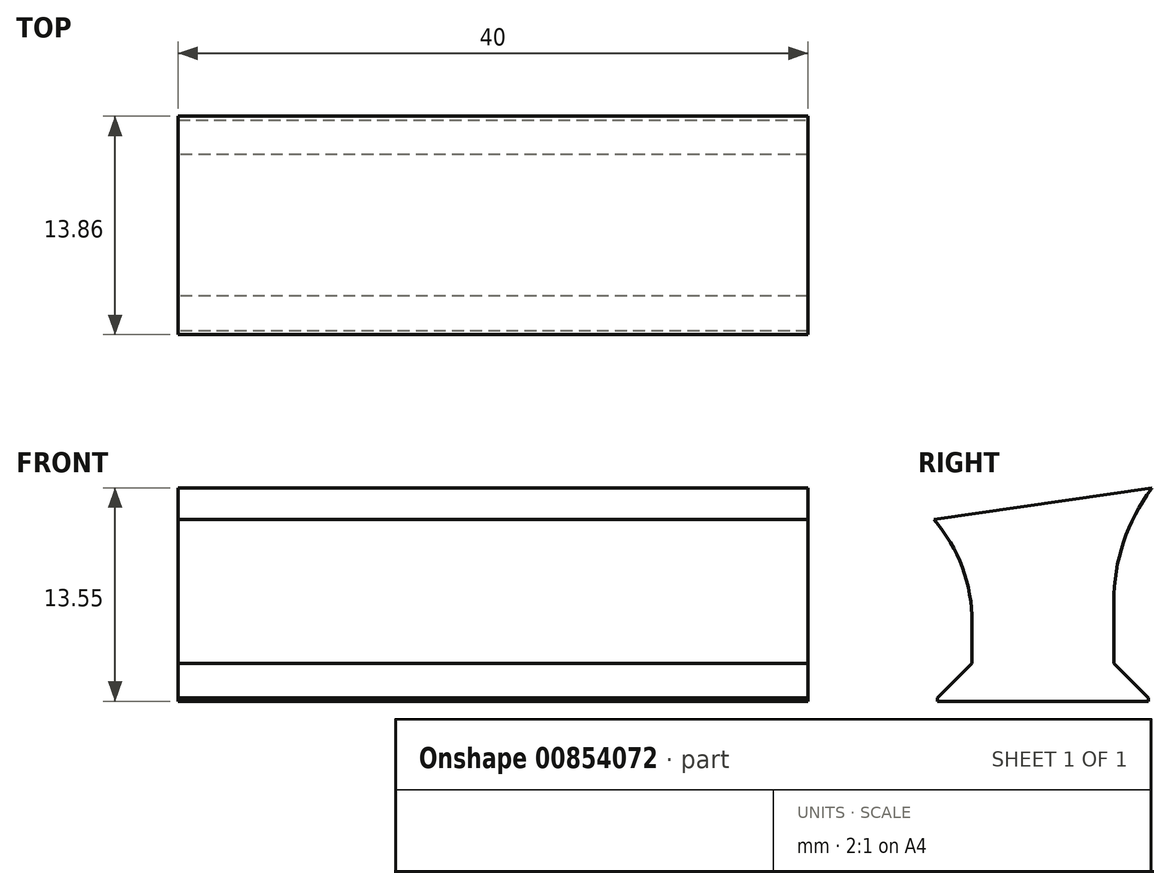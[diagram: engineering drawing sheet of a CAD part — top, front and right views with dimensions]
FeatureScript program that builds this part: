
annotation { "Feature Type Name" : "Feature", "Feature Type Description" : "" }
export const myFeature = defineFeature(function(context is Context, id is Id, definition is map)
    precondition{}
    {
        {
            var Q0;
            Q0=qCreatedBy(makeId("Top.planeOp"),FACE);
            var sketch = newSketch(context, id + "F0", { "sketchPlane" : qUnion([Q0])});
            skLineSegment(sketch, "E0.bottom", {"start": v(0, 0) * mm, "end": v(40, 0) * mm});
            skLineSegment(sketch, "E0.top", {"start": v(0, 13.4) * mm, "end": v(40, 13.4) * mm});
            skLineSegment(sketch, "E0.left", {"start": v(0, 0) * mm, "end": v(0, 13.4) * mm});
            skLineSegment(sketch, "E0.right", {"start": v(40, 0) * mm, "end": v(40, 13.4) * mm});
            skSolve(sketch);
        }
        {
            var Q0;
            Q0=makeQuery(id+"F0.imprint","IMPRINT",FACE,{"disambiguationData":[TD([[makeQuery(id+"F0.imprint","IMPRINT",EDGE,{"derivedFrom":sQuery(id+"F0.wireOp",EDGE,"E0.bottom")}),1.0]])]});
            extrude(context, id + "F1", {"entities" : qUnion([Q0]), "depth" : 2.4 * mm, "offsetDistance" : 25 * mm});
        }
        {
            var Q0;
            Q0=makeQuery(id+"F1.opExtrude","CAP_EDGE",EDGE,{"disambiguationData":[OSD([sQuery(id+"F0.wireOp",EDGE,"E0.top")])],"isStart":false});
            var Q1;
            Q1=makeQuery(id+"F1.opExtrude","CAP_EDGE",EDGE,{"disambiguationData":[OSD([sQuery(id+"F0.wireOp",EDGE,"E0.bottom")])],"isStart":false});
            chamfer(context, id + "F2", {"entities" : qUnion([Q0, Q1]), "width" : 2.2 * mm, "tangentPropagation" : true});
        }
        {
            var Q0;
            Q0=makeQuery(id+"F1.opExtrude","CAP_FACE",FACE,{"disambiguationData":[OSD([sQuery(id+"F0.wireOp",EDGE,"E0.bottom"),sQuery(id+"F0.wireOp",EDGE,"E0.top"),sQuery(id+"F0.wireOp",EDGE,"E0.left"),sQuery(id+"F0.wireOp",EDGE,"E0.right")])],"isStart":false});
            extrude(context, id + "F3", {"entities" : qUnion([Q0]), "operationType" : NewBodyOperationType.ADD, "depth" : 10.8 * mm, "offsetDistance" : 25 * mm});
        }
        {
            var Q0;
            {var subQ0=sQuery(id+"F0.wireOp",EDGE,"E0.right");var subQ1=sQuery(id+"F0.wireOp",EDGE,"E0.left");var subQ2=sQuery(id+"F0.wireOp",EDGE,"E0.top");var subQ3=sQuery(id+"F0.wireOp",EDGE,"E0.bottom");Q0=makeQuery(id+"F3.opExtrude","CAP_EDGE",EDGE,{"disambiguationData":[OSD([subQ3,subQ2,subQ1,subQ0]),TDD([makeQuery(id+"F2.opChamfer","BLEND_EDGE",EDGE,{"blendedFrom":[makeQuery(id+"F1.opExtrude","CAP_EDGE",EDGE,{"disambiguationData":[OSD([subQ3])],"isStart":false}),makeQuery(id+"F1.opExtrude","CAP_FACE",FACE,{"disambiguationData":[OSD([subQ3,subQ2,subQ1,subQ0])],"isStart":false})],"blendedInto":[makeQuery(id+"F1.opExtrude","CAP_FACE",FACE,{"disambiguationData":[OSD([subQ3,subQ2,subQ1,subQ0])],"isStart":false})]})])],"isStart":false});}
            chamfer(context, id + "F4", {"entities" : qUnion([Q0]), "chamferType" : ChamferType.TWO_OFFSETS, "width1" : 9 * mm, "oppositeDirection" : false, "width2" : 1.3 * mm, "tangentPropagation" : true});
        }
        {
            var Q0;
            Q0=makeQuery(id+"F4.opChamfer","BLEND_FACE",FACE,{"disambiguationData":[OSD([sQuery(id+"F0.wireOp",EDGE,"E0.bottom"),sQuery(id+"F0.wireOp",EDGE,"E0.top"),sQuery(id+"F0.wireOp",EDGE,"E0.left"),sQuery(id+"F0.wireOp",EDGE,"E0.right")])]});
            var sketch = newSketch(context, id + "F5", { "sketchPlane" : qUnion([Q0])});
            skLineSegment(sketch, "E1.bottom", {"start": v(0, 15.43) * mm, "end": v(40, 15.43) * mm});
            skLineSegment(sketch, "E1.top", {"start": v(0, 1.43) * mm, "end": v(40, 1.43) * mm});
            skLineSegment(sketch, "E1.left", {"start": v(0, 15.43) * mm, "end": v(0, 1.43) * mm});
            skLineSegment(sketch, "E1.right", {"start": v(40, 15.43) * mm, "end": v(40, 1.43) * mm});
            skSolve(sketch);
        }
        {
            var Q0;
            {var subQ0=sQuery(id+"F5.wireOp",EDGE,"E1.top");Q0=makeQuery(id+"F5.imprint","IMPRINT",FACE,{"disambiguationData":[TD([[makeQuery(id+"F5.imprint","IMPRINT",EDGE,{"derivedFrom":subQ0}),1.0]])]});}
            var Q1;
            {var subQ1=sQuery(id+"F0.wireOp",EDGE,"E0.right");var subQ2=sQuery(id+"F0.wireOp",EDGE,"E0.left");var subQ3=sQuery(id+"F0.wireOp",EDGE,"E0.top");var subQ4=sQuery(id+"F0.wireOp",EDGE,"E0.bottom");var subQ5=makeQuery(id+"F1.opExtrude","CAP_FACE",FACE,{"disambiguationData":[OSD([subQ4,subQ3,subQ2,subQ1])],"isStart":false});var subQ6=makeQuery(id+"F2.opChamfer","BLEND_EDGE",EDGE,{"blendedFrom":[makeQuery(id+"F1.opExtrude","CAP_EDGE",EDGE,{"disambiguationData":[OSD([subQ4])],"isStart":false}),subQ5],"blendedInto":[subQ5]});var subQ7=makeQuery(id+"F3.opExtrude","CAP_EDGE",EDGE,{"disambiguationData":[OSD([subQ4,subQ3,subQ2,subQ1]),TDD([subQ6])],"isStart":false});var subQ8=makeQuery(id+"F4.opChamfer","BLEND_EDGE",EDGE,{"blendedFrom":[subQ7,makeQuery(id+"F3.opExtrude","SWEPT_FACE",FACE,{"disambiguationData":[OSD([subQ4,subQ3,subQ2,subQ1]),TDD([subQ6])]})],"blendedInto":[makeQuery(id+"F3.opExtrude","SWEPT_FACE",FACE,{"disambiguationData":[OSD([subQ4,subQ3,subQ2,subQ1]),TDD([subQ6])]})]});Q1=makeQuery(id+"F5.imprint","IMPRINT",FACE,{"disambiguationData":[TD([[makeQuery(id+"F5.imprint","IMPRINT",EDGE,{"derivedFrom":subQ8}),-1.0]])]});}
            var Q2;
            {var subQ0=sQuery(id+"F5.wireOp",EDGE,"E1.bottom");Q2=makeQuery(id+"F5.imprint","IMPRINT",FACE,{"disambiguationData":[TD([[makeQuery(id+"F5.imprint","IMPRINT",EDGE,{"derivedFrom":subQ0}),-1.0]])]});}
            extrude(context, id + "F6", {"entities" : qUnion([Q0, Q1, Q2]), "operationType" : NewBodyOperationType.ADD, "depth" : -3 * mm, "offsetDistance" : 25 * mm});
        }
        {
            var Q0;
            Q0=makeQuery(id+"F6.opExtrude","CAP_EDGE",EDGE,{"disambiguationData":[OSD([sQuery(id+"F5.wireOp",EDGE,"E1.bottom")])],"isStart":false});
            chamfer(context, id + "F7", {"entities" : qUnion([Q0]), "width" : 3 * mm, "tangentPropagation" : true});
        }
        {
            var Q0;
            Q0=makeQuery(id+"F6.opExtrude","CAP_EDGE",EDGE,{"disambiguationData":[OSD([sQuery(id+"F5.wireOp",EDGE,"E1.top")])],"isStart":false});
            chamfer(context, id + "F8", {"entities" : qUnion([Q0]), "chamferType" : ChamferType.TWO_OFFSETS, "width1" : 3 * mm, "oppositeDirection" : false, "width2" : 2.02 * mm, "tangentPropagation" : true});
        }
        {
            var Q0;
            {var subQ0=sQuery(id+"F0.wireOp",EDGE,"E0.right");var subQ1=sQuery(id+"F0.wireOp",EDGE,"E0.left");var subQ2=sQuery(id+"F0.wireOp",EDGE,"E0.top");var subQ3=sQuery(id+"F0.wireOp",EDGE,"E0.bottom");Q0=makeQuery(id+"F7.opChamfer","BLEND_EDGE",EDGE,{"blendedFrom":[makeQuery(id+"F6.opExtrude","CAP_EDGE",EDGE,{"disambiguationData":[OSD([sQuery(id+"F5.wireOp",EDGE,"E1.bottom")])],"isStart":false}),makeQuery(id+"F3.opExtrude","SWEPT_FACE",FACE,{"disambiguationData":[OSD([subQ3,subQ2,subQ1,subQ0]),TDD([makeQuery(id+"F2.opChamfer","BLEND_EDGE",EDGE,{"blendedFrom":[makeQuery(id+"F1.opExtrude","CAP_EDGE",EDGE,{"disambiguationData":[OSD([subQ2])],"isStart":false}),makeQuery(id+"F1.opExtrude","CAP_FACE",FACE,{"disambiguationData":[OSD([subQ3,subQ2,subQ1,subQ0])],"isStart":false})],"blendedInto":[makeQuery(id+"F1.opExtrude","CAP_FACE",FACE,{"disambiguationData":[OSD([subQ3,subQ2,subQ1,subQ0])],"isStart":false})]})])]})],"blendedInto":[makeQuery(id+"F3.opExtrude","SWEPT_FACE",FACE,{"disambiguationData":[OSD([subQ3,subQ2,subQ1,subQ0]),TDD([makeQuery(id+"F2.opChamfer","BLEND_EDGE",EDGE,{"blendedFrom":[makeQuery(id+"F1.opExtrude","CAP_EDGE",EDGE,{"disambiguationData":[OSD([subQ2])],"isStart":false}),makeQuery(id+"F1.opExtrude","CAP_FACE",FACE,{"disambiguationData":[OSD([subQ3,subQ2,subQ1,subQ0])],"isStart":false})],"blendedInto":[makeQuery(id+"F1.opExtrude","CAP_FACE",FACE,{"disambiguationData":[OSD([subQ3,subQ2,subQ1,subQ0])],"isStart":false})]})])]})]});}
            fillet(context, id + "F9", {"entities" : qUnion([Q0]), "radius" : 12 * mm, "tangentPropagation" : true, "allowEdgeOverflow" : false});
        }
        {
            var Q0;
            {var subQ0=sQuery(id+"F0.wireOp",EDGE,"E0.right");var subQ1=sQuery(id+"F0.wireOp",EDGE,"E0.left");var subQ2=sQuery(id+"F0.wireOp",EDGE,"E0.top");var subQ3=sQuery(id+"F0.wireOp",EDGE,"E0.bottom");Q0=makeQuery(id+"F8.opChamfer","BLEND_EDGE",EDGE,{"blendedFrom":[makeQuery(id+"F6.opExtrude","CAP_EDGE",EDGE,{"disambiguationData":[OSD([sQuery(id+"F5.wireOp",EDGE,"E1.top")])],"isStart":false}),makeQuery(id+"F3.opExtrude","SWEPT_FACE",FACE,{"disambiguationData":[OSD([subQ3,subQ2,subQ1,subQ0]),TDD([makeQuery(id+"F2.opChamfer","BLEND_EDGE",EDGE,{"blendedFrom":[makeQuery(id+"F1.opExtrude","CAP_EDGE",EDGE,{"disambiguationData":[OSD([subQ3])],"isStart":false}),makeQuery(id+"F1.opExtrude","CAP_FACE",FACE,{"disambiguationData":[OSD([subQ3,subQ2,subQ1,subQ0])],"isStart":false})],"blendedInto":[makeQuery(id+"F1.opExtrude","CAP_FACE",FACE,{"disambiguationData":[OSD([subQ3,subQ2,subQ1,subQ0])],"isStart":false})]})])]})],"blendedInto":[makeQuery(id+"F3.opExtrude","SWEPT_FACE",FACE,{"disambiguationData":[OSD([subQ3,subQ2,subQ1,subQ0]),TDD([makeQuery(id+"F2.opChamfer","BLEND_EDGE",EDGE,{"blendedFrom":[makeQuery(id+"F1.opExtrude","CAP_EDGE",EDGE,{"disambiguationData":[OSD([subQ3])],"isStart":false}),makeQuery(id+"F1.opExtrude","CAP_FACE",FACE,{"disambiguationData":[OSD([subQ3,subQ2,subQ1,subQ0])],"isStart":false})],"blendedInto":[makeQuery(id+"F1.opExtrude","CAP_FACE",FACE,{"disambiguationData":[OSD([subQ3,subQ2,subQ1,subQ0])],"isStart":false})]})])]})]});}
            fillet(context, id + "F10", {"entities" : qUnion([Q0]), "radius" : 10 * mm, "tangentPropagation" : true, "allowEdgeOverflow" : false});
        }
    });
